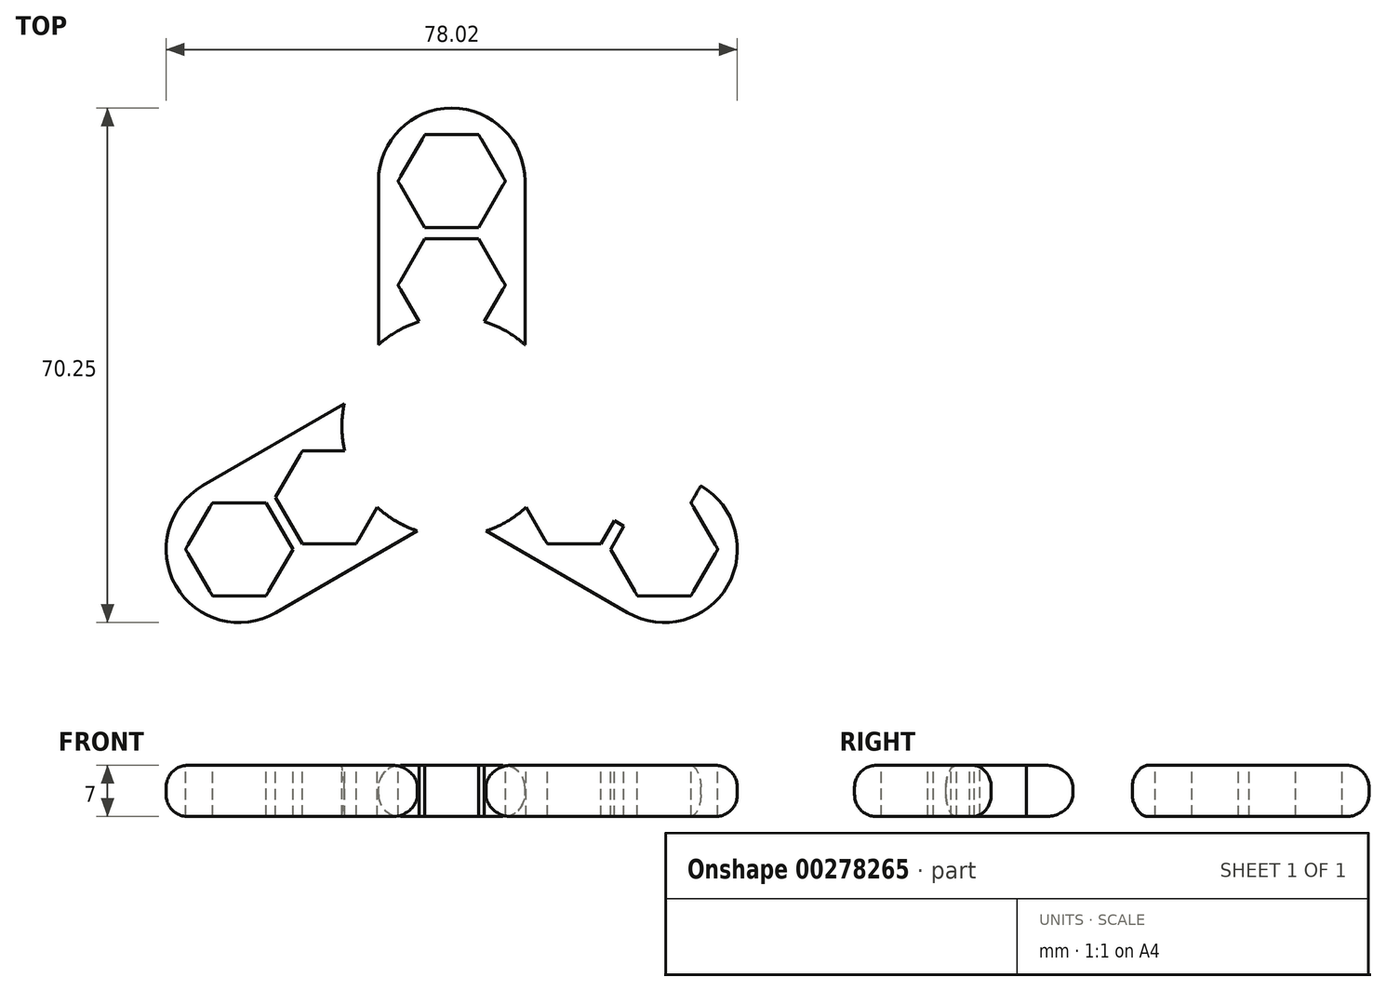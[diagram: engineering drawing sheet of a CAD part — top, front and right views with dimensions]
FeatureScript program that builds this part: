
annotation { "Feature Type Name" : "Feature", "Feature Type Description" : "" }
export const myFeature = defineFeature(function(context is Context, id is Id, definition is map)
    precondition{}
    {
        {
            var Q0;
            Q0=qCreatedBy(makeId("Top.planeOp"),FACE);
            var sketch = newSketch(context, id + "F0", { "sketchPlane" : qUnion([Q0])});
            skArc(sketch, "E0", {"start": v(-10, 11.17) * mm, "mid": v(-12.94, 7.58) * mm, "end": v(-14.64, 3.26) * mm});
            skArc(sketch, "E1", {"start": v(10, 33.5) * mm, "mid": v(0, 43.5) * mm, "end": v(-10, 33.5) * mm});
            skCircle(sketch, "E2.cCircle", {"center": v(0, 33.5) * mm, "radius": 6.35 * mm, "construction": true});
            skLineSegment(sketch, "E2.0", {"start": v(-3.67, 39.85) * mm, "end": v(3.67, 39.85) * mm});
            skLineSegment(sketch, "E2.1", {"start": v(3.67, 39.85) * mm, "end": v(7.33, 33.5) * mm});
            skLineSegment(sketch, "E2.2", {"start": v(7.33, 33.5) * mm, "end": v(3.67, 27.15) * mm});
            skLineSegment(sketch, "E2.3", {"start": v(3.67, 27.15) * mm, "end": v(-3.67, 27.15) * mm});
            skLineSegment(sketch, "E2.4", {"start": v(-3.67, 27.15) * mm, "end": v(-7.33, 33.5) * mm});
            skLineSegment(sketch, "E2.5", {"start": v(-7.33, 33.5) * mm, "end": v(-3.67, 39.85) * mm});
            skPoint(sketch, "E2.0.midPoint", {"position": v(0, 39.85) * mm});
            skPoint(sketch, "E3", {"position": v(-10, 33.5) * mm});
            skPoint(sketch, "E4", {"position": v(10, 33.5) * mm});
            skLineSegment(sketch, "E5", {"start": v(-10, 33.5) * mm, "end": v(10, 33.5) * mm});
            skLineSegment(sketch, "E6", {"start": v(10, 33.5) * mm, "end": v(10, 11.17) * mm});
            skLineSegment(sketch, "E7", {"start": v(-10, 33.5) * mm, "end": v(-10, 11.17) * mm});
            skArc(sketch, "E8.2.5", {"start": v(14.77, 2.6) * mm, "mid": v(13.1, 7.29) * mm, "end": v(10, 11.17) * mm});
            skLineSegment(sketch, "E9", {"start": v(0, 0) * mm, "end": v(0, 33.5) * mm});
            skCircle(sketch, "E10", {"center": v(0, 0) * mm, "radius": 11.12 * mm});
            skCircle(sketch, "E11", {"center": v(0, 0) * mm, "radius": 15 * mm});
            skCircle(sketch, "E12.cCircle", {"center": v(0, 19.3) * mm, "radius": 6.35 * mm, "construction": true});
            skLineSegment(sketch, "E12.0", {"start": v(-3.67, 25.65) * mm, "end": v(3.67, 25.65) * mm});
            skLineSegment(sketch, "E12.1", {"start": v(3.67, 25.65) * mm, "end": v(7.33, 19.3) * mm});
            skLineSegment(sketch, "E12.2", {"start": v(7.33, 19.3) * mm, "end": v(3.67, 12.95) * mm});
            skLineSegment(sketch, "E12.3", {"start": v(3.67, 12.95) * mm, "end": v(-3.67, 12.95) * mm});
            skLineSegment(sketch, "E12.4", {"start": v(-3.67, 12.95) * mm, "end": v(-7.33, 19.3) * mm});
            skLineSegment(sketch, "E12.5", {"start": v(-7.33, 19.3) * mm, "end": v(-3.67, 25.65) * mm});
            skPoint(sketch, "E12.0.midPoint", {"position": v(0, 25.65) * mm});
            skLineSegment(sketch, "E13", {"start": v(0, 27.15) * mm, "end": v(0, 25.65) * mm});
            skLineSegment(sketch, "E14", {"start": v(0, 33.5) * mm, "end": v(0, 0) * mm});
            skLineSegment(sketch, "E15", {"start": v(0, 0) * mm, "end": v(3.36, 0) * mm});
            skCircle(sketch, "E16.1.1", {"center": v(-16.71, -9.65) * mm, "radius": 6.35 * mm, "construction": true});
            skPoint(sketch, "E16.1.2", {"position": v(-34.51, -19.92) * mm});
            skLineSegment(sketch, "E16.1.3", {"start": v(-9.38, -9.65) * mm, "end": v(-13.05, -16) * mm});
            skPoint(sketch, "E16.1.4", {"position": v(-22.21, -12.82) * mm});
            skPoint(sketch, "E16.1.5", {"position": v(-24.01, -25.41) * mm});
            skLineSegment(sketch, "E16.1.6", {"start": v(-13.05, -16) * mm, "end": v(-20.38, -16) * mm});
            skPoint(sketch, "E16.1.7", {"position": v(-34.01, -8.09) * mm});
            skPoint(sketch, "E16.1.8", {"position": v(-29.01, -16.75) * mm});
            skArc(sketch, "E16.1.9", {"start": v(-34.01, -8.09) * mm, "mid": v(-37.67, -21.75) * mm, "end": v(-24.01, -25.41) * mm});
            skCircle(sketch, "E16.1.10", {"center": v(-29.01, -16.75) * mm, "radius": 6.35 * mm, "construction": true});
            skLineSegment(sketch, "E16.1.11", {"start": v(-36.34, -16.75) * mm, "end": v(-32.68, -10.4) * mm});
            skLineSegment(sketch, "E16.1.13", {"start": v(-21.68, -16.75) * mm, "end": v(-25.35, -23.1) * mm});
            skLineSegment(sketch, "E16.1.14", {"start": v(-25.35, -23.1) * mm, "end": v(-32.68, -23.1) * mm});
            skLineSegment(sketch, "E16.1.15", {"start": v(-24.01, -25.41) * mm, "end": v(-34.01, -8.09) * mm});
            skLineSegment(sketch, "E16.1.16", {"start": v(-34.01, -8.09) * mm, "end": v(-14.68, 3.07) * mm});
            skLineSegment(sketch, "E16.1.17", {"start": v(-24.01, -25.41) * mm, "end": v(-4.68, -14.25) * mm});
            skArc(sketch, "E16.1.18", {"start": v(-4.68, -14.25) * mm, "mid": v(-0.1, -15) * mm, "end": v(4.5, -14.3) * mm});
            skLineSegment(sketch, "E16.1.19", {"start": v(0, 0) * mm, "end": v(-29.01, -16.75) * mm});
            skPoint(sketch, "E16.1.21", {"position": v(-29.01, -16.75) * mm});
            skLineSegment(sketch, "E16.1.22", {"start": v(-24.05, -9.65) * mm, "end": v(-20.38, -3.3) * mm});
            skLineSegment(sketch, "E16.1.23", {"start": v(-20.38, -3.3) * mm, "end": v(-13.05, -3.3) * mm});
            skLineSegment(sketch, "E16.1.24", {"start": v(-13.05, -3.3) * mm, "end": v(-9.38, -9.65) * mm});
            skLineSegment(sketch, "E16.1.25", {"start": v(0, 0) * mm, "end": v(-1.68, 2.91) * mm});
            skLineSegment(sketch, "E16.1.26", {"start": v(-29.01, -16.75) * mm, "end": v(0, 0) * mm});
            skArc(sketch, "E16.1.28", {"start": v(-4.68, -14.25) * mm, "mid": v(-0.1, -15) * mm, "end": v(4.5, -14.3) * mm});
            skLineSegment(sketch, "E16.1.29", {"start": v(-32.68, -23.1) * mm, "end": v(-36.34, -16.75) * mm});
            skLineSegment(sketch, "E16.1.30", {"start": v(-32.68, -10.4) * mm, "end": v(-25.35, -10.4) * mm});
            skLineSegment(sketch, "E16.1.31", {"start": v(-25.35, -10.4) * mm, "end": v(-21.68, -16.75) * mm});
            skArc(sketch, "E16.1.32", {"start": v(-9.63, 11.5) * mm, "mid": v(-12.86, 7.7) * mm, "end": v(-14.68, 3.07) * mm});
            skLineSegment(sketch, "E16.1.33", {"start": v(-20.38, -16) * mm, "end": v(-24.05, -9.65) * mm});
            skLineSegment(sketch, "E16.1.34", {"start": v(-23.51, -13.58) * mm, "end": v(-22.21, -12.82) * mm});
            skArc(sketch, "E16.1.36", {"start": v(-9.63, 11.5) * mm, "mid": v(-12.86, 7.7) * mm, "end": v(-14.68, 3.07) * mm});
            skArc(sketch, "E16.1.37", {"start": v(-4.68, -14.25) * mm, "mid": v(-0.1, -15) * mm, "end": v(4.5, -14.3) * mm});
            skArc(sketch, "E16.1.39", {"start": v(-9.63, 11.5) * mm, "mid": v(-12.86, 7.7) * mm, "end": v(-14.68, 3.07) * mm});
            skCircle(sketch, "E16.2.1", {"center": v(16.71, -9.65) * mm, "radius": 6.35 * mm, "construction": true});
            skPoint(sketch, "E16.2.2", {"position": v(34.51, -19.93) * mm});
            skLineSegment(sketch, "E16.2.3", {"start": v(13.05, -3.3) * mm, "end": v(20.38, -3.3) * mm});
            skPoint(sketch, "E16.2.4", {"position": v(22.21, -12.83) * mm});
            skPoint(sketch, "E16.2.5", {"position": v(34.01, -8.09) * mm});
            skLineSegment(sketch, "E16.2.6", {"start": v(20.38, -3.3) * mm, "end": v(24.05, -9.65) * mm});
            skPoint(sketch, "E16.2.7", {"position": v(24.01, -25.41) * mm});
            skPoint(sketch, "E16.2.8", {"position": v(29.01, -16.75) * mm});
            skArc(sketch, "E16.2.9", {"start": v(24.01, -25.41) * mm, "mid": v(37.67, -21.75) * mm, "end": v(34.01, -8.09) * mm});
            skCircle(sketch, "E16.2.10", {"center": v(29.01, -16.75) * mm, "radius": 6.35 * mm, "construction": true});
            skLineSegment(sketch, "E16.2.11", {"start": v(32.68, -23.1) * mm, "end": v(25.35, -23.1) * mm});
            skLineSegment(sketch, "E16.2.13", {"start": v(25.35, -10.4) * mm, "end": v(32.68, -10.4) * mm});
            skLineSegment(sketch, "E16.2.14", {"start": v(32.68, -10.4) * mm, "end": v(36.34, -16.75) * mm});
            skLineSegment(sketch, "E16.2.15", {"start": v(34.01, -8.09) * mm, "end": v(24.01, -25.41) * mm});
            skLineSegment(sketch, "E16.2.16", {"start": v(24.01, -25.41) * mm, "end": v(4.68, -14.25) * mm});
            skLineSegment(sketch, "E16.2.17", {"start": v(34.01, -8.09) * mm, "end": v(14.68, 3.07) * mm});
            skArc(sketch, "E16.2.18", {"start": v(14.68, 3.07) * mm, "mid": v(13.03, 7.42) * mm, "end": v(10.14, 11.05) * mm});
            skLineSegment(sketch, "E16.2.19", {"start": v(0, 0) * mm, "end": v(29.01, -16.75) * mm});
            skPoint(sketch, "E16.2.21", {"position": v(29.01, -16.75) * mm});
            skLineSegment(sketch, "E16.2.22", {"start": v(20.38, -16) * mm, "end": v(13.05, -16) * mm});
            skLineSegment(sketch, "E16.2.23", {"start": v(13.05, -16) * mm, "end": v(9.38, -9.65) * mm});
            skLineSegment(sketch, "E16.2.24", {"start": v(9.38, -9.65) * mm, "end": v(13.05, -3.3) * mm});
            skLineSegment(sketch, "E16.2.25", {"start": v(0, 0) * mm, "end": v(-1.68, -2.91) * mm});
            skLineSegment(sketch, "E16.2.26", {"start": v(29.01, -16.75) * mm, "end": v(0, 0) * mm});
            skArc(sketch, "E16.2.28", {"start": v(14.68, 3.07) * mm, "mid": v(13.03, 7.42) * mm, "end": v(10.14, 11.05) * mm});
            skLineSegment(sketch, "E16.2.29", {"start": v(36.34, -16.75) * mm, "end": v(32.68, -23.1) * mm});
            skLineSegment(sketch, "E16.2.30", {"start": v(25.35, -23.1) * mm, "end": v(21.68, -16.75) * mm});
            skLineSegment(sketch, "E16.2.31", {"start": v(21.68, -16.75) * mm, "end": v(25.35, -10.4) * mm});
            skArc(sketch, "E16.2.32", {"start": v(-5.14, -14.09) * mm, "mid": v(-0.24, -15) * mm, "end": v(4.68, -14.25) * mm});
            skLineSegment(sketch, "E16.2.33", {"start": v(24.05, -9.65) * mm, "end": v(20.38, -16) * mm});
            skLineSegment(sketch, "E16.2.34", {"start": v(23.51, -13.58) * mm, "end": v(22.21, -12.83) * mm});
            skArc(sketch, "E16.2.36", {"start": v(-5.14, -14.09) * mm, "mid": v(-0.24, -15) * mm, "end": v(4.68, -14.25) * mm});
            skArc(sketch, "E16.2.37", {"start": v(14.68, 3.07) * mm, "mid": v(13.03, 7.42) * mm, "end": v(10.14, 11.05) * mm});
            skArc(sketch, "E16.2.39", {"start": v(-5.14, -14.09) * mm, "mid": v(-0.24, -15) * mm, "end": v(4.68, -14.25) * mm});
            skArc(sketch, "E17", {"start": v(-14.68, 3.07) * mm, "mid": v(-11.7, 6.75) * mm, "end": v(-10, 11.17) * mm});
            skArc(sketch, "E18", {"start": v(10, 11.17) * mm, "mid": v(11.7, 6.75) * mm, "end": v(14.68, 3.07) * mm});
            skArc(sketch, "E19", {"start": v(4.68, -14.25) * mm, "mid": v(0, -13.5) * mm, "end": v(-4.68, -14.25) * mm});
            skSolve(sketch);
        }
        {
            var Q0;
            Q0=sQuery(id+"F0.wireOp",EDGE,"E15");
            extrude(context, id + "F1", {"bodyType" : ExtendedToolBodyType.SURFACE, "surfaceEntities" : qUnion([Q0]), "depth" : 5 * mm, "offsetDistance" : 25 * mm});
        }
        {
            var Q0;
            {var subQ2=sQuery(id+"F0.wireOp",EDGE,"E16.1.6");Q0=makeQuery(id+"F0.imprint","IMPRINT",FACE,{"disambiguationData":[TD([[makeQuery(id+"F0.imprint","IMPRINT",EDGE,{"derivedFrom":subQ2}),1.0]])]});}
            var Q1;
            {var subQ8=sQuery(id+"F0.wireOp",EDGE,"E16.1.16");Q1=makeQuery(id+"F0.imprint","IMPRINT",FACE,{"disambiguationData":[TD([[makeQuery(id+"F0.imprint","IMPRINT",EDGE,{"derivedFrom":subQ8}),-1.0]])]});}
            var Q2;
            {var subQ2=sQuery(id+"F0.wireOp",EDGE,"E16.2.16");Q2=makeQuery(id+"F0.imprint","IMPRINT",FACE,{"disambiguationData":[TD([[makeQuery(id+"F0.imprint","IMPRINT",EDGE,{"derivedFrom":subQ2}),-1.0]])]});}
            var Q3;
            {var subQ2=sQuery(id+"F0.wireOp",EDGE,"E2.2");Q3=makeQuery(id+"F0.imprint","IMPRINT",FACE,{"disambiguationData":[TD([[makeQuery(id+"F0.imprint","IMPRINT",EDGE,{"derivedFrom":subQ2}),1.0]])]});}
            var Q4;
            {var subQ2=sQuery(id+"F0.wireOp",EDGE,"E2.4");Q4=makeQuery(id+"F0.imprint","IMPRINT",FACE,{"disambiguationData":[TD([[makeQuery(id+"F0.imprint","IMPRINT",EDGE,{"derivedFrom":subQ2}),1.0]])]});}
            var Q5;
            {var subQ0=sQuery(id+"F0.wireOp",EDGE,"E16.2.6");Q5=makeQuery(id+"F0.imprint","IMPRINT",FACE,{"disambiguationData":[TD([[makeQuery(id+"F0.imprint","IMPRINT",EDGE,{"derivedFrom":subQ0}),1.0]])]});}
            var Q6;
            {var subQ1=sQuery(id+"F0.wireOp",EDGE,"E16.2.9");Q6=makeQuery(id+"F0.imprint","IMPRINT",FACE,{"disambiguationData":[TD([[makeQuery(id+"F0.imprint","IMPRINT",EDGE,{"derivedFrom":subQ1}),1.0]])]});}
            var Q7;
            {var subQ10=sQuery(id+"F0.wireOp",EDGE,"E11");var subQ11=makeQuery(id+"F0.imprint","IMPRINT",VERTEX,{"disambiguationData":[OD(0.0)],"derivedFrom":subQ10});Q7=makeQuery(id+"F0.imprint","IMPRINT",FACE,{"disambiguationData":[TD([[makeQuery(id+"F0.imprint","IMPRINT",EDGE,{"disambiguationData":[TD([[subQ11,-1.0]])],"derivedFrom":subQ10}),1.0]])]});}
            var Q8;
            {var subQ2=sQuery(id+"F0.wireOp",EDGE,"E1");Q8=makeQuery(id+"F0.imprint","IMPRINT",FACE,{"disambiguationData":[TD([[makeQuery(id+"F0.imprint","IMPRINT",EDGE,{"derivedFrom":subQ2}),1.0]])]});}
            var Q9;
            {var subQ1=sQuery(id+"F0.wireOp",EDGE,"E16.1.9");Q9=makeQuery(id+"F0.imprint","IMPRINT",FACE,{"disambiguationData":[TD([[makeQuery(id+"F0.imprint","IMPRINT",EDGE,{"derivedFrom":subQ1}),1.0]])]});}
            var Q10;
            {var subQ0=sQuery(id+"F0.wireOp",EDGE,"E11");var subQ13=makeQuery(id+"F0.imprint","IMPRINT",VERTEX,{"disambiguationData":[OD(2.0)],"derivedFrom":subQ0});Q10=makeQuery(id+"F0.imprint","IMPRINT",FACE,{"disambiguationData":[TD([[makeQuery(id+"F0.imprint","IMPRINT",EDGE,{"disambiguationData":[TD([[subQ13,1.0]])],"derivedFrom":subQ0}),1.0]])]});}
            var Q11;
            {var subQ5=sQuery(id+"F0.wireOp",EDGE,"E11");var subQ14=makeQuery(id+"F0.imprint","IMPRINT",VERTEX,{"disambiguationData":[OD(1.0)],"derivedFrom":subQ5});Q11=makeQuery(id+"F0.imprint","IMPRINT",FACE,{"disambiguationData":[TD([[makeQuery(id+"F0.imprint","IMPRINT",EDGE,{"disambiguationData":[TD([[subQ14,1.0]])],"derivedFrom":subQ5}),1.0]])]});}
            extrude(context, id + "F2", {"entities" : qUnion([Q0, Q1, Q2, Q3, Q4, Q5, Q6, Q7, Q8, Q9, Q10, Q11]), "oppositeDirection" : true, "depth" : 7 * mm, "offsetDistance" : 25 * mm});
        }
        {
            var Q0;
            Q0=makeQuery(id+"F2.opExtrude","CAP_EDGE",EDGE,{"disambiguationData":[OSD([sQuery(id+"F0.wireOp",EDGE,"E18")])],"isStart":true});
            var Q1;
            Q1=makeQuery(id+"F2.opExtrude","CAP_EDGE",EDGE,{"disambiguationData":[OSD([sQuery(id+"F0.wireOp",EDGE,"E16.2.17")])],"isStart":true});
            var Q2;
            Q2=makeQuery(id+"F2.opExtrude","CAP_EDGE",EDGE,{"disambiguationData":[OSD([sQuery(id+"F0.wireOp",EDGE,"E6")])],"isStart":true});
            var Q3;
            Q3=makeQuery(id+"F2.opExtrude","CAP_EDGE",EDGE,{"disambiguationData":[OSD([sQuery(id+"F0.wireOp",EDGE,"E18")])],"isStart":false});
            var Q4;
            Q4=makeQuery(id+"F2.opExtrude","CAP_EDGE",EDGE,{"disambiguationData":[OSD([sQuery(id+"F0.wireOp",EDGE,"E6")])],"isStart":false});
            var Q5;
            Q5=makeQuery(id+"F2.opExtrude","CAP_EDGE",EDGE,{"disambiguationData":[OSD([sQuery(id+"F0.wireOp",EDGE,"E16.2.17")])],"isStart":false});
            var Q6;
            Q6=makeQuery(id+"F2.opExtrude","CAP_EDGE",EDGE,{"disambiguationData":[OSD([sQuery(id+"F0.wireOp",EDGE,"E7")])],"isStart":false});
            var Q7;
            Q7=makeQuery(id+"F2.opExtrude","CAP_EDGE",EDGE,{"disambiguationData":[OSD([sQuery(id+"F0.wireOp",EDGE,"E16.2.9")])],"isStart":false});
            var Q8;
            Q8=makeQuery(id+"F2.opExtrude","CAP_EDGE",EDGE,{"disambiguationData":[OSD([sQuery(id+"F0.wireOp",EDGE,"E16.2.9")])],"isStart":true});
            var Q9;
            Q9=makeQuery(id+"F2.opExtrude","CAP_EDGE",EDGE,{"disambiguationData":[OSD([sQuery(id+"F0.wireOp",EDGE,"E16.2.16")])],"isStart":true});
            var Q10;
            Q10=makeQuery(id+"F2.opExtrude","CAP_EDGE",EDGE,{"disambiguationData":[OSD([sQuery(id+"F0.wireOp",EDGE,"E16.2.16")])],"isStart":false});
            var Q11;
            Q11=makeQuery(id+"F2.opExtrude","CAP_EDGE",EDGE,{"disambiguationData":[OSD([sQuery(id+"F0.wireOp",EDGE,"E19")])],"isStart":true});
            var Q12;
            Q12=makeQuery(id+"F2.opExtrude","CAP_EDGE",EDGE,{"disambiguationData":[OSD([sQuery(id+"F0.wireOp",EDGE,"E19")])],"isStart":false});
            var Q13;
            Q13=makeQuery(id+"F2.opExtrude","CAP_EDGE",EDGE,{"disambiguationData":[OSD([sQuery(id+"F0.wireOp",EDGE,"E16.1.17")])],"isStart":false});
            var Q14;
            Q14=makeQuery(id+"F2.opExtrude","CAP_EDGE",EDGE,{"disambiguationData":[OSD([sQuery(id+"F0.wireOp",EDGE,"E16.1.9")])],"isStart":true});
            var Q15;
            Q15=makeQuery(id+"F2.opExtrude","CAP_EDGE",EDGE,{"disambiguationData":[OSD([sQuery(id+"F0.wireOp",EDGE,"E16.1.9")])],"isStart":false});
            var Q16;
            Q16=makeQuery(id+"F2.opExtrude","CAP_EDGE",EDGE,{"disambiguationData":[OSD([sQuery(id+"F0.wireOp",EDGE,"E16.1.16")])],"isStart":true});
            var Q17;
            Q17=makeQuery(id+"F2.opExtrude","CAP_EDGE",EDGE,{"disambiguationData":[OSD([sQuery(id+"F0.wireOp",EDGE,"E17")])],"isStart":true});
            var Q18;
            Q18=makeQuery(id+"F2.opExtrude","CAP_EDGE",EDGE,{"disambiguationData":[OSD([sQuery(id+"F0.wireOp",EDGE,"E7")])],"isStart":true});
            var Q19;
            Q19=makeQuery(id+"F2.opExtrude","CAP_EDGE",EDGE,{"disambiguationData":[OSD([sQuery(id+"F0.wireOp",EDGE,"E17")])],"isStart":false});
            var Q20;
            Q20=makeQuery(id+"F2.opExtrude","CAP_EDGE",EDGE,{"disambiguationData":[OSD([sQuery(id+"F0.wireOp",EDGE,"E16.1.16")])],"isStart":false});
            var Q21;
            Q21=makeQuery(id+"F2.opExtrude","CAP_EDGE",EDGE,{"disambiguationData":[OSD([sQuery(id+"F0.wireOp",EDGE,"E1")])],"isStart":false});
            var Q22;
            Q22=makeQuery(id+"F2.opExtrude","CAP_EDGE",EDGE,{"disambiguationData":[OSD([sQuery(id+"F0.wireOp",EDGE,"E1")])],"isStart":true});
            var Q23;
            Q23=makeQuery(id+"F2.opExtrude","CAP_EDGE",EDGE,{"disambiguationData":[OSD([sQuery(id+"F0.wireOp",EDGE,"E16.1.17")])],"isStart":true});
            fillet(context, id + "F3", {"entities" : qUnion([Q0, Q1, Q2, Q3, Q4, Q5, Q6, Q7, Q8, Q9, Q10, Q11, Q12, Q13, Q14, Q15, Q16, Q17, Q18, Q19, Q20, Q21, Q22, Q23]), "radius" : 3 * mm, "allowEdgeOverflow" : false});
        }
    });
